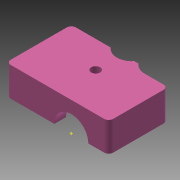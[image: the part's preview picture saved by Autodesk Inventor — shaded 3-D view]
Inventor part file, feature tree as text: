
AUTODESK INVENTOR PART (.ipt)
format: ipt  version: 2014 (Build 180170000, 170)  size: 176,128 bytes
history: native  units: mm
features: sketch x7, extrude x6, fillet x2, other x2, hole x1, plane x1
ambient origin geometry x8: Origin, YZ Plane, XZ Plane, XY Plane, X Axis, Y Axis, Z Axis, Center Point
bodies: Solid1 (feature_tree)
feature tree (19):
  extrude  "Extrusion1"  Depth=36.2mm
  hole  "Hole1"  [1 undecoded]
  extrude  "Extrusion2"  Depth=13.5mm
  extrude  "Extrusion3"  Depth=6.0mm
  extrude  "Extrusion5"  Depth=5.31mm
  fillet  "Fillet1"  Radius=1.5mm
  fillet  "Fillet2"  Radius=10.32mm
  extrude  "Extrusion4"  Depth=6.0mm
  extrude  "Extrusion6"  Depth=10.0mm
  plane  "Work Plane1"
  sketch  "Sketch1"  dims[d0=36.2mm d1=23.0mm]
  sketch  "Sketch2"  dims[d2=10.32mm d3=0.0mm d4=3.0mm]
  sketch  "Sketch3"  dims[d5=18.1mm d6=13.5mm]
  sketch  "Sketch4"  dims[d7=3.2mm d8=6.0mm d9=6.3mm d10=2.0mm d11=90.0deg d12=8.0mm d13=20.594885mm d14=3.2mm]
  sketch  "Sketch5"  dims[d15=21.0mm d16=5.31mm d17=1.5mm d18=10.32mm d19=0.0mm]
  sketch  "Sketch6"  dims[d20=26.0mm d21=6.0mm]
  sketch  "Sketch7"  dims[d22=4.7mm d23=0.0mm d24=2.0mm d25=4.7mm d26=0.0mm d27=5.75mm d28=20.0mm d29=4.13mm d30=8.73mm d31=0.0mm d32=1.5875mm d33=1.5875mm d34=12.0mm d35=10.0mm d36=0.0mm]
  other  "Work Axis1"
  other  "Work Point1"
note: 1 required parameter value undecoded (feature->parameter linkage not recoverable at this tier; creation-order binding heuristic only, values carry confidence <= 0.55)
